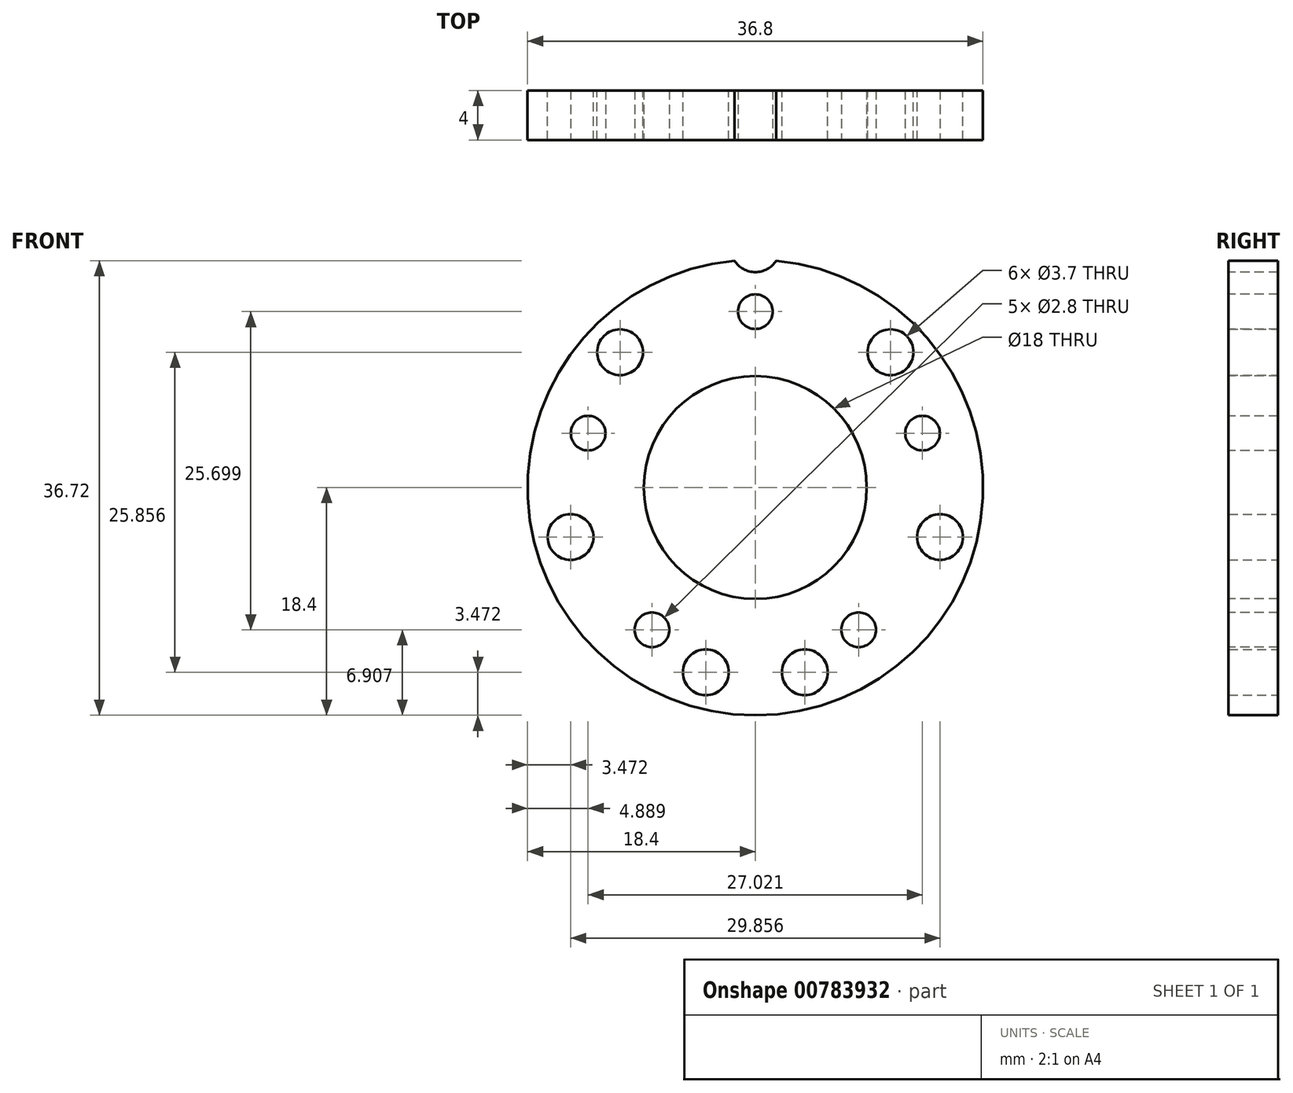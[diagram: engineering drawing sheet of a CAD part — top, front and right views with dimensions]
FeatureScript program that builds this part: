
annotation { "Feature Type Name" : "Feature", "Feature Type Description" : "" }
export const myFeature = defineFeature(function(context is Context, id is Id, definition is map)
    precondition{}
    {
        {
            var Q0;
            Q0=qCreatedBy(makeId("Front.planeOp"),FACE);
            var sketch = newSketch(context, id + "F0", { "sketchPlane" : qUnion([Q0])});
            skCircle(sketch, "E0", {"center": v(0, 0) * mm, "radius": 18.4 * mm});
            skCircle(sketch, "E1", {"center": v(0, 0) * mm, "radius": 9 * mm});
            skCircle(sketch, "E2.cCircle", {"center": v(0, 0) * mm, "radius": 14.2 * mm, "construction": true});
            skLineSegment(sketch, "E2.0", {"start": v(0, 14.2) * mm, "end": v(13.51, 4.39) * mm, "construction": true});
            skLineSegment(sketch, "E2.1", {"start": v(13.51, 4.39) * mm, "end": v(8.35, -11.5) * mm, "construction": true});
            skLineSegment(sketch, "E2.2", {"start": v(8.35, -11.5) * mm, "end": v(-8.35, -11.5) * mm, "construction": true});
            skLineSegment(sketch, "E2.3", {"start": v(-8.35, -11.5) * mm, "end": v(-13.51, 4.39) * mm, "construction": true});
            skLineSegment(sketch, "E2.4", {"start": v(-13.51, 4.39) * mm, "end": v(0, 14.2) * mm, "construction": true});
            skCircle(sketch, "E3", {"center": v(0, 14.2) * mm, "radius": 1.4 * mm});
            skCircle(sketch, "E4", {"center": v(13.51, 4.39) * mm, "radius": 1.4 * mm});
            skCircle(sketch, "E5", {"center": v(8.35, -11.5) * mm, "radius": 1.4 * mm});
            skCircle(sketch, "E6", {"center": v(-8.35, -11.5) * mm, "radius": 1.4 * mm});
            skCircle(sketch, "E7", {"center": v(-13.51, 4.39) * mm, "radius": 1.4 * mm});
            skSolve(sketch);
        }
        {
            var Q0;
            Q0=makeQuery(id+"F0.imprint","IMPRINT",FACE,{"disambiguationData":[TD([[makeQuery(id+"F0.imprint","IMPRINT",EDGE,{"derivedFrom":sQuery(id+"F0.wireOp",EDGE,"E0")}),1.0]])]});
            extrude(context, id + "F1", {"entities" : qUnion([Q0]), "oppositeDirection" : true, "depth" : 4 * mm, "offsetDistance" : 25 * mm});
        }
        {
            var Q0;
            Q0=makeQuery(id+"F1.opExtrude","CAP_FACE",FACE,{"disambiguationData":[OSD([sQuery(id+"F0.wireOp",EDGE,"E0"),sQuery(id+"F0.wireOp",EDGE,"E1"),sQuery(id+"F0.wireOp",EDGE,"E3"),sQuery(id+"F0.wireOp",EDGE,"E4"),sQuery(id+"F0.wireOp",EDGE,"E5"),sQuery(id+"F0.wireOp",EDGE,"E6"),sQuery(id+"F0.wireOp",EDGE,"E7")])],"isStart":false});
            var sketch = newSketch(context, id + "F2", { "sketchPlane" : qUnion([Q0])});
            skCircle(sketch, "E8.cCircle", {"center": v(0, 0) * mm, "radius": 15.45 * mm, "construction": true});
            skLineSegment(sketch, "E8.0", {"start": v(4, 14.93) * mm, "end": v(10.93, 10.93) * mm, "construction": true});
            skLineSegment(sketch, "E8.1", {"start": v(10.93, 10.93) * mm, "end": v(14.93, 4) * mm, "construction": true});
            skLineSegment(sketch, "E8.2", {"start": v(14.93, 4) * mm, "end": v(14.93, -4) * mm, "construction": true});
            skLineSegment(sketch, "E8.3", {"start": v(14.93, -4) * mm, "end": v(10.93, -10.93) * mm, "construction": true});
            skLineSegment(sketch, "E8.4", {"start": v(10.93, -10.93) * mm, "end": v(4, -14.93) * mm, "construction": true});
            skLineSegment(sketch, "E8.5", {"start": v(4, -14.93) * mm, "end": v(-4, -14.93) * mm, "construction": true});
            skLineSegment(sketch, "E8.6", {"start": v(-4, -14.93) * mm, "end": v(-10.93, -10.93) * mm, "construction": true});
            skLineSegment(sketch, "E8.7", {"start": v(-10.93, -10.93) * mm, "end": v(-14.93, -4) * mm, "construction": true});
            skLineSegment(sketch, "E8.8", {"start": v(-14.93, -4) * mm, "end": v(-14.93, 4) * mm, "construction": true});
            skLineSegment(sketch, "E8.9", {"start": v(-14.93, 4) * mm, "end": v(-10.93, 10.93) * mm, "construction": true});
            skLineSegment(sketch, "E8.10", {"start": v(-10.93, 10.93) * mm, "end": v(-4, 14.93) * mm, "construction": true});
            skLineSegment(sketch, "E8.11", {"start": v(-4, 14.93) * mm, "end": v(4, 14.93) * mm, "construction": true});
            skLineSegment(sketch, "E9", {"start": v(0, 0) * mm, "end": v(0, -14.93) * mm, "construction": true});
            skCircle(sketch, "E10", {"center": v(-10.93, 10.93) * mm, "radius": 1.85 * mm});
            skCircle(sketch, "E11", {"center": v(10.93, 10.93) * mm, "radius": 1.85 * mm});
            skCircle(sketch, "E12", {"center": v(14.93, -4) * mm, "radius": 1.85 * mm});
            skCircle(sketch, "E13", {"center": v(4, -14.93) * mm, "radius": 1.85 * mm});
            skCircle(sketch, "E14", {"center": v(-4, -14.93) * mm, "radius": 1.85 * mm});
            skCircle(sketch, "E15", {"center": v(-14.93, -4) * mm, "radius": 1.85 * mm});
            skSolve(sketch);
        }
        {
            var Q0;
            Q0=makeQuery(id+"F2.imprint","IMPRINT",FACE,{"disambiguationData":[TD([[makeQuery(id+"F2.imprint","IMPRINT",EDGE,{"derivedFrom":sQuery(id+"F2.wireOp",EDGE,"E15")}),1.0]])]});
            var Q1;
            Q1=makeQuery(id+"F2.imprint","IMPRINT",FACE,{"disambiguationData":[TD([[makeQuery(id+"F2.imprint","IMPRINT",EDGE,{"derivedFrom":sQuery(id+"F2.wireOp",EDGE,"E10")}),1.0]])]});
            var Q2;
            Q2=makeQuery(id+"F2.imprint","IMPRINT",FACE,{"disambiguationData":[TD([[makeQuery(id+"F2.imprint","IMPRINT",EDGE,{"derivedFrom":sQuery(id+"F2.wireOp",EDGE,"E12")}),1.0]])]});
            var Q3;
            Q3=makeQuery(id+"F2.imprint","IMPRINT",FACE,{"disambiguationData":[TD([[makeQuery(id+"F2.imprint","IMPRINT",EDGE,{"derivedFrom":sQuery(id+"F2.wireOp",EDGE,"E11")}),1.0]])]});
            var Q4;
            Q4=makeQuery(id+"F2.imprint","IMPRINT",FACE,{"disambiguationData":[TD([[makeQuery(id+"F2.imprint","IMPRINT",EDGE,{"derivedFrom":sQuery(id+"F2.wireOp",EDGE,"E13")}),1.0]])]});
            var Q5;
            Q5=makeQuery(id+"F2.imprint","IMPRINT",FACE,{"disambiguationData":[TD([[makeQuery(id+"F2.imprint","IMPRINT",EDGE,{"derivedFrom":sQuery(id+"F2.wireOp",EDGE,"E14")}),1.0]])]});
            extrude(context, id + "F3", {"entities" : qUnion([Q0, Q1, Q2, Q3, Q4, Q5]), "operationType" : NewBodyOperationType.REMOVE, "oppositeDirection" : true, "depth" : 25 * mm, "offsetDistance" : 25 * mm});
        }
        {
            var Q0;
            Q0=makeQuery(id+"F1.opExtrude","CAP_FACE",FACE,{"disambiguationData":[OSD([sQuery(id+"F0.wireOp",EDGE,"E0"),sQuery(id+"F0.wireOp",EDGE,"E1"),sQuery(id+"F0.wireOp",EDGE,"E3"),sQuery(id+"F0.wireOp",EDGE,"E4"),sQuery(id+"F0.wireOp",EDGE,"E5"),sQuery(id+"F0.wireOp",EDGE,"E6"),sQuery(id+"F0.wireOp",EDGE,"E7")])],"isStart":true});
            var sketch = newSketch(context, id + "F4", { "sketchPlane" : qUnion([Q0])});
            skCircle(sketch, "E16", {"center": v(0, 19.4) * mm, "radius": 2 * mm});
            skSolve(sketch);
        }
        {
            var Q0;
            {var subQ0=sQuery(id+"F4.wireOp",EDGE,"E16");var subQ1=makeQuery(id+"F1.opExtrude","CAP_EDGE",EDGE,{"disambiguationData":[OSD([sQuery(id+"F0.wireOp",EDGE,"E0")])],"isStart":true});var subQ2=makeQuery(id+"F4.imprint","INTERSECT",VERTEX,{"disambiguationData":[OD(0.0)],"derivedFrom":[subQ1,subQ0]});Q0=makeQuery(id+"F4.imprint","IMPRINT",FACE,{"disambiguationData":[TD([[makeQuery(id+"F4.imprint","IMPRINT",EDGE,{"disambiguationData":[TD([[subQ2,-1.0]])],"derivedFrom":subQ0}),1.0]])]});}
            extrude(context, id + "F5", {"entities" : qUnion([Q0]), "operationType" : NewBodyOperationType.REMOVE, "oppositeDirection" : true, "depth" : 25 * mm, "offsetDistance" : 25 * mm});
        }
    });
